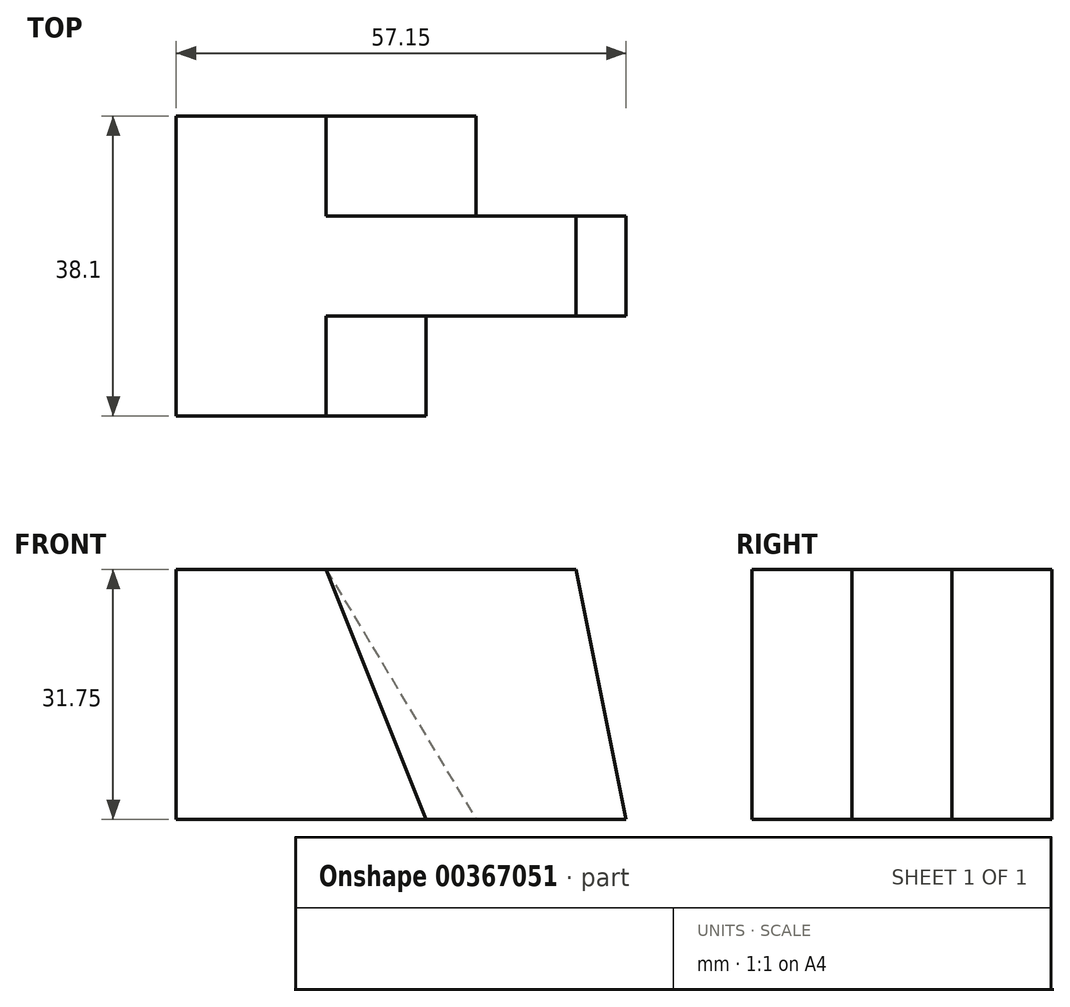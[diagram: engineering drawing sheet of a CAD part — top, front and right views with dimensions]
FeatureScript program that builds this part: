
annotation { "Feature Type Name" : "Feature", "Feature Type Description" : "" }
export const myFeature = defineFeature(function(context is Context, id is Id, definition is map)
    precondition{}
    {
        {
            var Q0;
            Q0=qCreatedBy(makeId("Front.planeOp"),FACE);
            var sketch = newSketch(context, id + "F0", { "sketchPlane" : qUnion([Q0])});
            skLineSegment(sketch, "E0", {"start": v(0, 0) * mm, "end": v(57.15, 0) * mm});
            skLineSegment(sketch, "E1", {"start": v(57.15, 0) * mm, "end": v(57.15, 31.75) * mm});
            skLineSegment(sketch, "E2", {"start": v(57.15, 31.75) * mm, "end": v(0, 31.75) * mm});
            skLineSegment(sketch, "E3", {"start": v(0, 31.75) * mm, "end": v(0, 0) * mm});
            skSolve(sketch);
        }
        {
            var Q0;
            Q0 = qSketchRegion(id + "F0", true);
            extrude(context, id + "F1", {"entities" : qUnion([Q0]), "depth" : 38.1 * mm});
        }
        {
            var Q0;
            Q0=makeQuery(id+"F1.opExtrude","CAP_FACE",FACE,{"disambiguationData":[OSD([sQuery(id+"F0.wireOp",EDGE,"E0"),sQuery(id+"F0.wireOp",EDGE,"E1"),sQuery(id+"F0.wireOp",EDGE,"E2"),sQuery(id+"F0.wireOp",EDGE,"E3")])],"isStart":false});
            var sketch = newSketch(context, id + "F2", { "sketchPlane" : qUnion([Q0])});
            skLineSegment(sketch, "E4", {"start": v(19.05, 31.75) * mm, "end": v(31.75, 0) * mm});
            skSolve(sketch);
        }
        {
            var Q0;
            {var subQ0=sQuery(id+"F2.wireOp",EDGE,"E4");Q0=makeQuery(id+"F2.imprint","IMPRINT",FACE,{"disambiguationData":[TD([[makeQuery(id+"F2.imprint","IMPRINT",EDGE,{"derivedFrom":subQ0}),1.0]])]});}
            extrude(context, id + "F3", {"entities" : qUnion([Q0]), "operationType" : NewBodyOperationType.REMOVE, "oppositeDirection" : true, "depth" : 12.7 * mm});
        }
        {
            var Q0;
            Q0=makeQuery(id+"F3.boolean.opBoolean","COPY",FACE,{"derivedFrom":makeQuery(id+"F3.opExtrude","CAP_FACE",FACE,{"disambiguationData":[OSD([sQuery(id+"F0.wireOp",EDGE,"E0"),sQuery(id+"F0.wireOp",EDGE,"E1"),sQuery(id+"F0.wireOp",EDGE,"E2"),sQuery(id+"F2.wireOp",EDGE,"E4")])],"isStart":false})});
            var sketch = newSketch(context, id + "F4", { "sketchPlane" : qUnion([Q0])});
            skLineSegment(sketch, "E5", {"start": v(50.8, 31.75) * mm, "end": v(57.15, 0) * mm});
            skSolve(sketch);
        }
        {
            var Q0;
            {var subQ0=sQuery(id+"F4.wireOp",EDGE,"E5");Q0=makeQuery(id+"F4.imprint","IMPRINT",FACE,{"disambiguationData":[TD([[makeQuery(id+"F4.imprint","IMPRINT",EDGE,{"derivedFrom":subQ0}),1.0]])]});}
            extrude(context, id + "F5", {"entities" : qUnion([Q0]), "operationType" : NewBodyOperationType.REMOVE, "oppositeDirection" : true, "depth" : 12.7 * mm});
        }
        {
            var Q0;
            Q0=makeQuery(id+"F1.opExtrude","CAP_FACE",FACE,{"disambiguationData":[OSD([sQuery(id+"F0.wireOp",EDGE,"E0"),sQuery(id+"F0.wireOp",EDGE,"E1"),sQuery(id+"F0.wireOp",EDGE,"E2"),sQuery(id+"F0.wireOp",EDGE,"E3")])],"isStart":true});
            var sketch = newSketch(context, id + "F6", { "sketchPlane" : qUnion([Q0])});
            skLineSegment(sketch, "E6", {"start": v(-19.05, 31.75) * mm, "end": v(-38.1, 0) * mm});
            skSolve(sketch);
        }
        {
            var Q0;
            {var subQ0=sQuery(id+"F6.wireOp",EDGE,"E6");Q0=makeQuery(id+"F6.imprint","IMPRINT",FACE,{"disambiguationData":[TD([[makeQuery(id+"F6.imprint","IMPRINT",EDGE,{"derivedFrom":subQ0}),-1.0]])]});}
            extrude(context, id + "F7", {"entities" : qUnion([Q0]), "operationType" : NewBodyOperationType.REMOVE, "oppositeDirection" : true, "depth" : 12.7 * mm});
        }
    });
